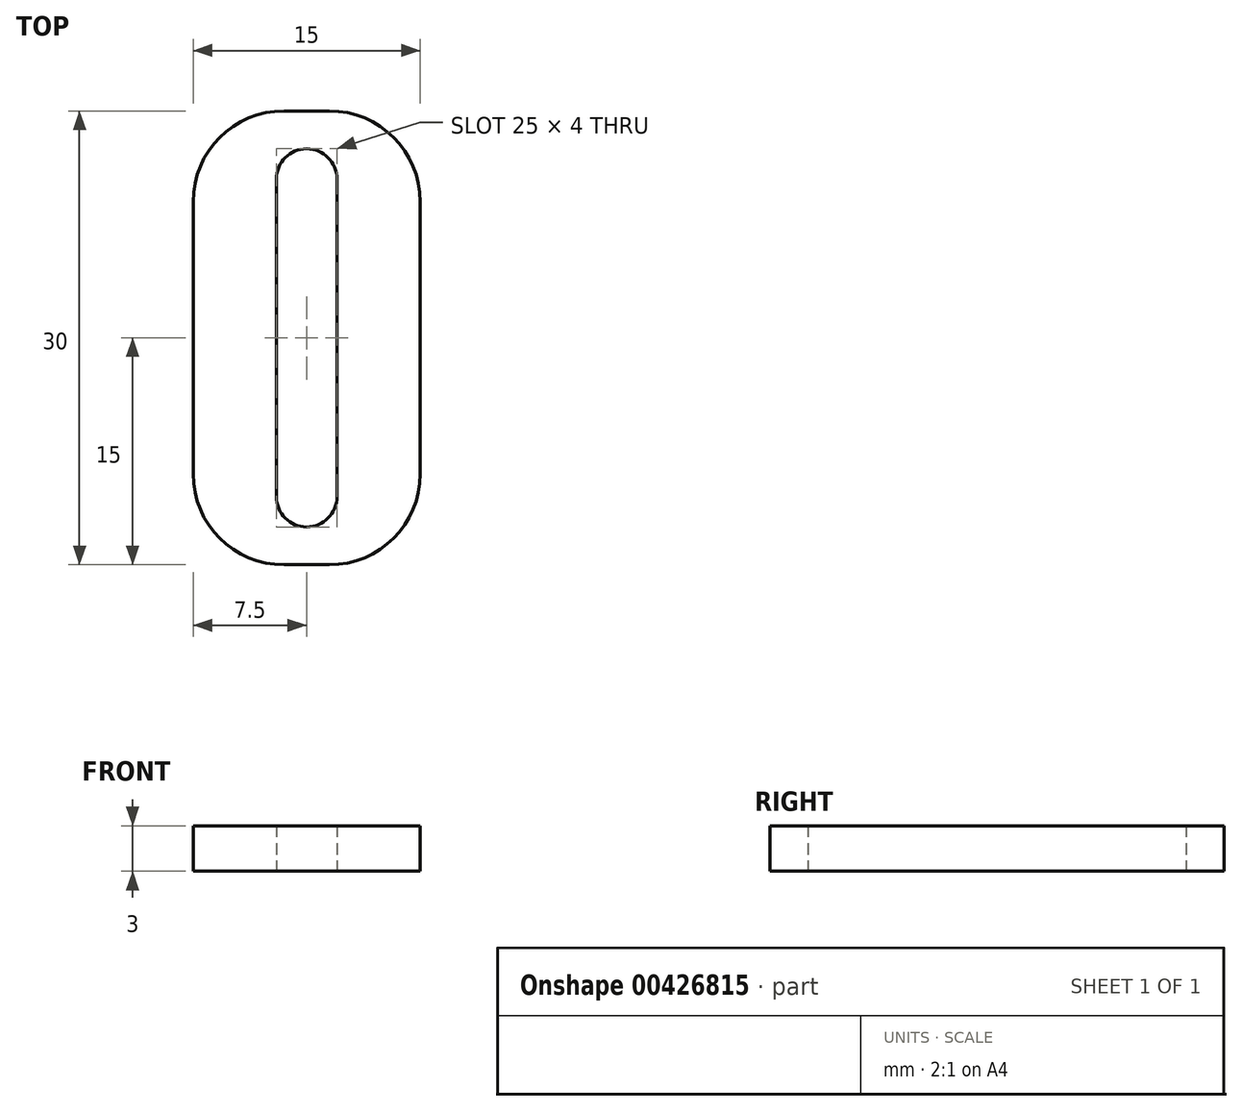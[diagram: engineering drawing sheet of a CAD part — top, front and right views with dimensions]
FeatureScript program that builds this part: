
annotation { "Feature Type Name" : "Feature", "Feature Type Description" : "" }
export const myFeature = defineFeature(function(context is Context, id is Id, definition is map)
    precondition{}
    {
        {
            var Q0;
            Q0=qCreatedBy(makeId("Top.planeOp"),FACE);
            var sketch = newSketch(context, id + "F0", { "sketchPlane" : qUnion([Q0])});
            skLineSegment(sketch, "E0.bottom", {"start": v(0, 0) * mm, "end": v(15, 0) * mm});
            skLineSegment(sketch, "E0.top", {"start": v(0, 30) * mm, "end": v(15, 30) * mm});
            skLineSegment(sketch, "E0.left", {"start": v(0, 0) * mm, "end": v(0, 30) * mm});
            skLineSegment(sketch, "E0.right", {"start": v(15, 0) * mm, "end": v(15, 30) * mm});
            skLineSegment(sketch, "E1", {"start": v(7.5, 25.19) * mm, "end": v(7.5, -9.37) * mm, "construction": true});
            skPoint(sketch, "E1.startSnap0", {"position": v(7.5, 30) * mm});
            skLineSegment(sketch, "E2", {"start": v(-2.96, 25.5) * mm, "end": v(22.72, 25.5) * mm, "construction": true});
            skLineSegment(sketch, "E3", {"start": v(-3.58, 4.5) * mm, "end": v(21.89, 4.5) * mm, "construction": true});
            skLineSegment(sketch, "E4", {"start": v(5.5, 22.78) * mm, "end": v(5.5, -5.84) * mm, "construction": true});
            skLineSegment(sketch, "E5", {"start": v(9.5, 23.03) * mm, "end": v(9.5, -5.5) * mm, "construction": true});
            skLineSegment(sketch, "E6", {"start": v(-1.5, 27.5) * mm, "end": v(17.7, 27.5) * mm, "construction": true});
            skLineSegment(sketch, "E7", {"start": v(-2.13, 2.5) * mm, "end": v(22.72, 2.5) * mm, "construction": true});
            skArc(sketch, "E8", {"start": v(9.5, 25.5) * mm, "mid": v(7.5, 27.5) * mm, "end": v(5.5, 25.5) * mm});
            skArc(sketch, "E9", {"start": v(5.5, 4.5) * mm, "mid": v(7.5, 2.5) * mm, "end": v(9.5, 4.5) * mm});
            skLineSegment(sketch, "E10", {"start": v(5.5, 25.5) * mm, "end": v(5.5, 4.5) * mm});
            skLineSegment(sketch, "E11", {"start": v(9.5, 4.5) * mm, "end": v(9.5, 25.5) * mm});
            skSolve(sketch);
        }
        {
            var Q0;
            Q0=makeQuery(id+"F0.imprint","IMPRINT",FACE,{"disambiguationData":[TD([[makeQuery(id+"F0.imprint","IMPRINT",EDGE,{"derivedFrom":sQuery(id+"F0.wireOp",EDGE,"E0.bottom")}),1.0]])]});
            extrude(context, id + "F1", {"entities" : qUnion([Q0]), "depth" : 3 * mm});
        }
        {
            var Q0;
            Q0=makeQuery(id+"F1.opExtrude","SWEPT_EDGE",EDGE,{"disambiguationData":[OSD([sQuery(id+"F0.wireOp",EDGE,"E0.bottom"),sQuery(id+"F0.wireOp",EDGE,"E0.right")])]});
            var Q1;
            Q1=makeQuery(id+"F1.opExtrude","SWEPT_EDGE",EDGE,{"disambiguationData":[OSD([sQuery(id+"F0.wireOp",EDGE,"E0.bottom"),sQuery(id+"F0.wireOp",EDGE,"E0.left")])]});
            var Q2;
            Q2=makeQuery(id+"F1.opExtrude","SWEPT_EDGE",EDGE,{"disambiguationData":[OSD([sQuery(id+"F0.wireOp",EDGE,"E0.top"),sQuery(id+"F0.wireOp",EDGE,"E0.right")])]});
            var Q3;
            Q3=makeQuery(id+"F1.opExtrude","SWEPT_EDGE",EDGE,{"disambiguationData":[OSD([sQuery(id+"F0.wireOp",EDGE,"E0.top"),sQuery(id+"F0.wireOp",EDGE,"E0.left")])]});
            fillet(context, id + "F2", {"entities" : qUnion([Q0, Q1, Q2, Q3]), "radius" : 6 * mm, "tangentPropagation" : true, "allowEdgeOverflow" : false});
        }
    });
